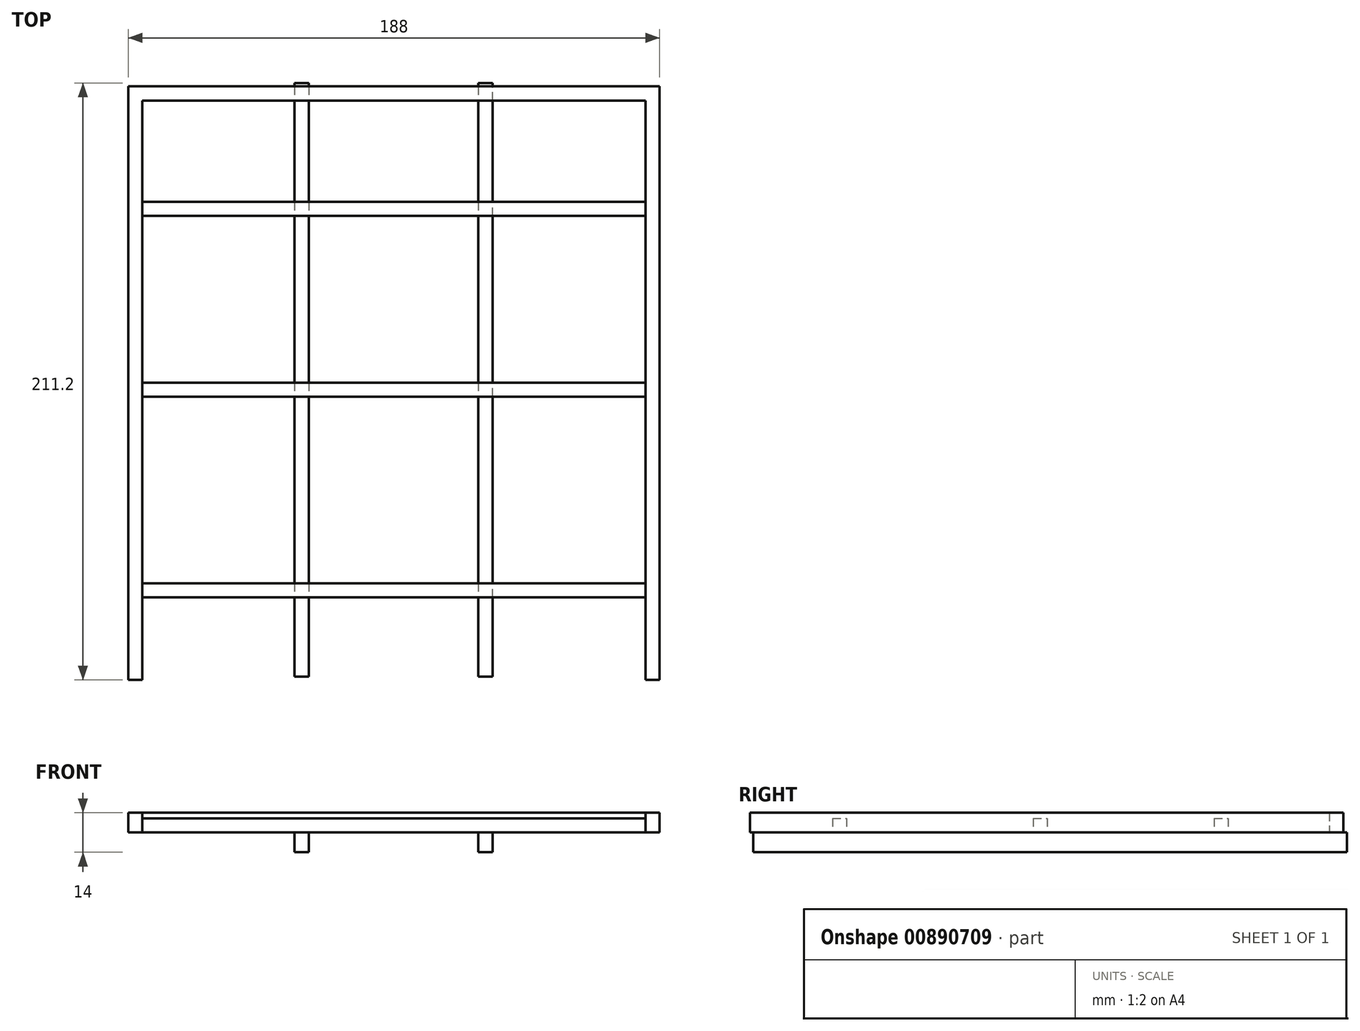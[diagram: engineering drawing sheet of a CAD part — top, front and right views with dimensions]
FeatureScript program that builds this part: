
annotation { "Feature Type Name" : "Feature", "Feature Type Description" : "" }
export const myFeature = defineFeature(function(context is Context, id is Id, definition is map)
    precondition{}
    {
        {
            var Q0;
            Q0=qCreatedBy(makeId("Top.planeOp"),FACE);
            var sketch = newSketch(context, id + "F0", { "sketchPlane" : qUnion([Q0])});
            skLineSegment(sketch, "E0.bottom", {"start": v(-93.9, 118.8) * mm, "end": v(94.1, 118.8) * mm});
            skLineSegment(sketch, "E0.top", {"start": v(-93.9, -91.2) * mm, "end": v(-88.9, -91.2) * mm});
            skLineSegment(sketch, "E0.left", {"start": v(-93.9, 118.8) * mm, "end": v(-93.9, -91.2) * mm});
            skLineSegment(sketch, "E0.right", {"start": v(94.1, 118.8) * mm, "end": v(94.1, -91.2) * mm});
            skLineSegment(sketch, "E1.top", {"start": v(-88.9, 113.8) * mm, "end": v(89.1, 113.8) * mm});
            skLineSegment(sketch, "E1.left", {"start": v(-88.9, -91.2) * mm, "end": v(-88.9, 113.8) * mm});
            skLineSegment(sketch, "E1.right", {"start": v(89.1, -91.2) * mm, "end": v(89.1, 113.8) * mm});
            skLineSegment(sketch, "E2.trimOffspring", {"start": v(89.1, -91.2) * mm, "end": v(94.1, -91.2) * mm});
            skSolve(sketch);
        }
        {
            var Q0;
            Q0 = qSketchRegion(id + "F0", true);
            extrude(context, id + "F1", {"entities" : qUnion([Q0]), "depth" : 7 * mm, "offsetDistance" : 25 * mm});
        }
        {
            var Q0;
            Q0=qCreatedBy(makeId("Top.planeOp"),FACE);
            var sketch = newSketch(context, id + "F2", { "sketchPlane" : qUnion([Q0])});
            skLineSegment(sketch, "E3.bottom", {"start": v(-89.9, 77.97) * mm, "end": v(90.1, 77.97) * mm});
            skLineSegment(sketch, "E3.top", {"start": v(-89.9, 72.97) * mm, "end": v(90.1, 72.97) * mm});
            skLineSegment(sketch, "E3.left", {"start": v(-89.9, 77.97) * mm, "end": v(-89.9, 72.97) * mm});
            skLineSegment(sketch, "E3.right", {"start": v(90.1, 77.97) * mm, "end": v(90.1, 72.97) * mm});
            skLineSegment(sketch, "E4.bottom", {"start": v(-89.9, 14) * mm, "end": v(90.1, 14) * mm});
            skLineSegment(sketch, "E4.top", {"start": v(-89.9, 9) * mm, "end": v(90.1, 9) * mm});
            skLineSegment(sketch, "E4.left", {"start": v(-89.9, 14) * mm, "end": v(-89.9, 9) * mm});
            skLineSegment(sketch, "E4.right", {"start": v(90.1, 14) * mm, "end": v(90.1, 9) * mm});
            skLineSegment(sketch, "E5.bottom", {"start": v(-89.9, -57) * mm, "end": v(90.1, -57) * mm});
            skLineSegment(sketch, "E5.top", {"start": v(-89.9, -62) * mm, "end": v(90.1, -62) * mm});
            skLineSegment(sketch, "E5.left", {"start": v(-89.9, -57) * mm, "end": v(-89.9, -62) * mm});
            skLineSegment(sketch, "E5.right", {"start": v(90.1, -57) * mm, "end": v(90.1, -62) * mm});
            skSolve(sketch);
        }
        {
            var Q0;
            Q0 = qSketchRegion(id + "F2", true);
            extrude(context, id + "F3", {"entities" : qUnion([Q0]), "operationType" : NewBodyOperationType.ADD, "depth" : 5 * mm, "offsetDistance" : 25 * mm});
        }
        {
            var Q0;
            Q0=qCreatedBy(makeId("Top.planeOp"),FACE);
            var sketch = newSketch(context, id + "F4", { "sketchPlane" : qUnion([Q0])});
            skLineSegment(sketch, "E6.0", {"start": v(-35, 120) * mm, "end": v(-35, -90) * mm});
            skLineSegment(sketch, "E7.0", {"start": v(-30, 120) * mm, "end": v(-30, -90) * mm});
            skLineSegment(sketch, "E8.0", {"start": v(30, 120) * mm, "end": v(30, -90) * mm});
            skLineSegment(sketch, "E9", {"start": v(-35, -90) * mm, "end": v(-30, -90) * mm});
            skLineSegment(sketch, "E10", {"start": v(30, -90) * mm, "end": v(35, -90) * mm});
            skLineSegment(sketch, "E11", {"start": v(35, -90) * mm, "end": v(35, 120) * mm});
            skLineSegment(sketch, "E12", {"start": v(35, 120) * mm, "end": v(30, 120) * mm});
            skLineSegment(sketch, "E13.trimOffspring", {"start": v(-30, 120) * mm, "end": v(-35, 120) * mm});
            skSolve(sketch);
        }
        {
            var Q0;
            Q0 = qSketchRegion(id + "F4", true);
            extrude(context, id + "F5", {"entities" : qUnion([Q0]), "operationType" : NewBodyOperationType.ADD, "oppositeDirection" : true, "depth" : 7 * mm, "offsetDistance" : 25 * mm});
        }
    });
